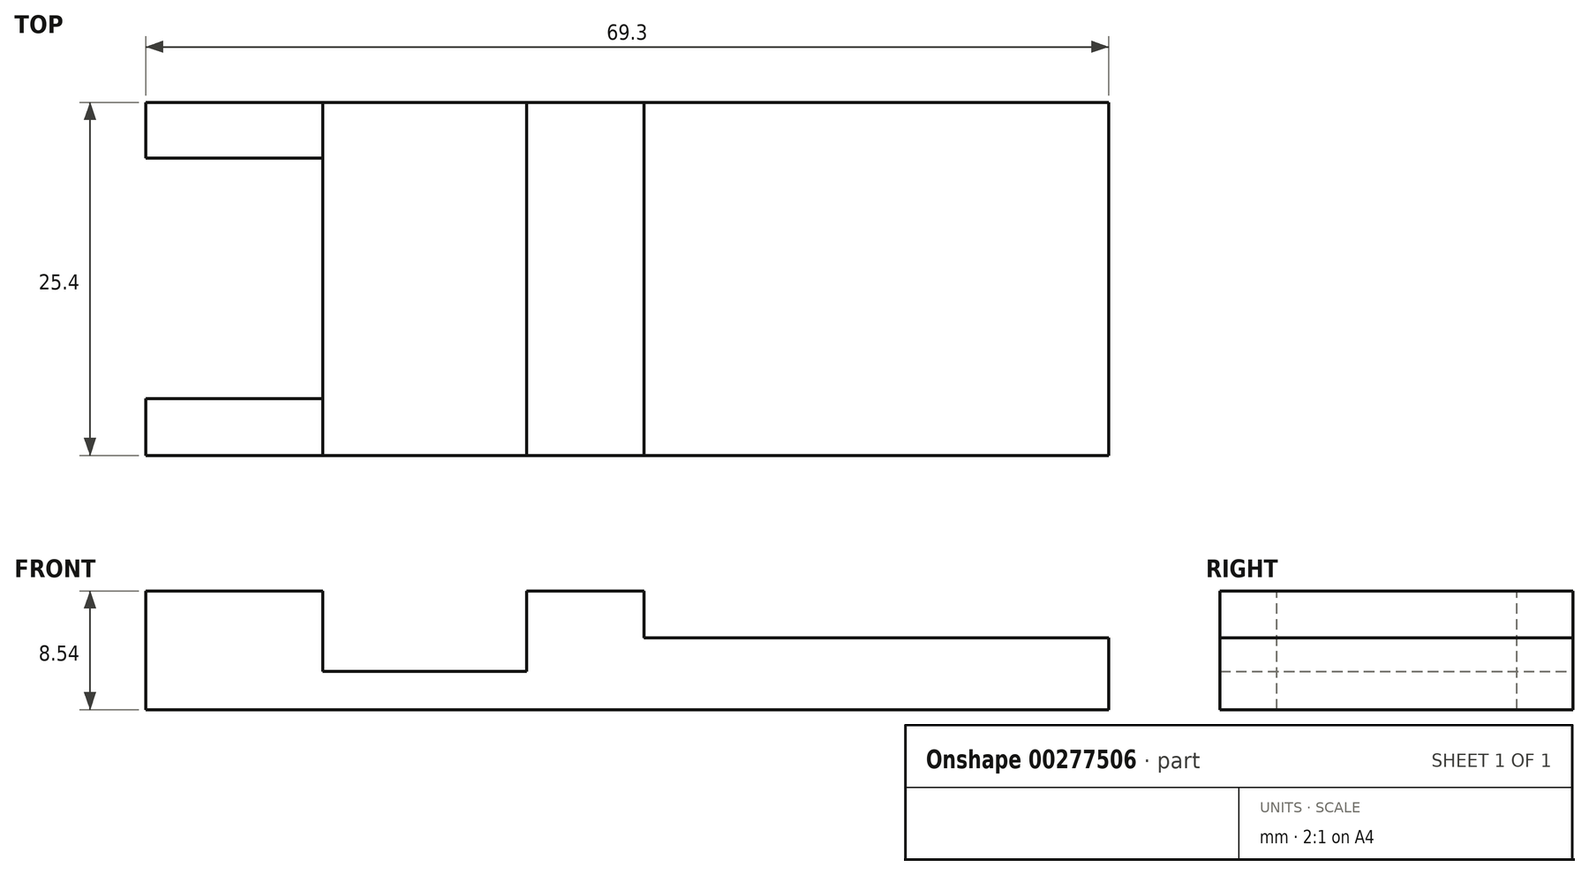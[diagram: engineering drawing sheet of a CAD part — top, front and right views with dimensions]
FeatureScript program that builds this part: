
annotation { "Feature Type Name" : "Feature", "Feature Type Description" : "" }
export const myFeature = defineFeature(function(context is Context, id is Id, definition is map)
    precondition{}
    {
        {
            var Q0;
            Q0=qCreatedBy(makeId("Front.planeOp"),FACE);
            var sketch = newSketch(context, id + "F0", { "sketchPlane" : qUnion([Q0])});
            skLineSegment(sketch, "E0", {"start": v(-49.57, 8.54) * mm, "end": v(-49.57, 0) * mm});
            skLineSegment(sketch, "E1", {"start": v(19.73, 0) * mm, "end": v(19.73, 5.17) * mm});
            skLineSegment(sketch, "E2", {"start": v(19.73, 5.17) * mm, "end": v(-13.72, 5.17) * mm});
            skLineSegment(sketch, "E3", {"start": v(-13.72, 5.17) * mm, "end": v(-13.72, 8.54) * mm});
            skLineSegment(sketch, "E4", {"start": v(-13.72, 8.54) * mm, "end": v(-22.15, 8.54) * mm});
            skLineSegment(sketch, "E5", {"start": v(-22.15, 8.54) * mm, "end": v(-22.15, 2.74) * mm});
            skLineSegment(sketch, "E6", {"start": v(-22.15, 2.74) * mm, "end": v(-36.82, 2.74) * mm});
            skLineSegment(sketch, "E7", {"start": v(-36.82, 2.74) * mm, "end": v(-36.82, 8.54) * mm});
            skLineSegment(sketch, "E8", {"start": v(-36.82, 8.54) * mm, "end": v(-49.57, 8.54) * mm});
            skLineSegment(sketch, "E9", {"start": v(-49.57, 0) * mm, "end": v(19.73, 0) * mm});
            skSolve(sketch);
        }
        {
            var Q0;
            Q0 = qSketchRegion(id + "F0", true);
            extrude(context, id + "F1", {"entities" : qUnion([Q0]), "depth" : 25.4 * mm});
        }
        {
            var Q0;
            Q0=qCreatedBy(makeId("Top.planeOp"),FACE);
            var sketch = newSketch(context, id + "F2", { "sketchPlane" : qUnion([Q0])});
            skLineSegment(sketch, "E10.bottom", {"start": v(-52.98, -4.03) * mm, "end": v(-36.84, -4.03) * mm});
            skLineSegment(sketch, "E10.top", {"start": v(-52.98, -21.32) * mm, "end": v(-36.84, -21.32) * mm});
            skLineSegment(sketch, "E10.left", {"start": v(-52.98, -4.03) * mm, "end": v(-52.98, -21.32) * mm});
            skLineSegment(sketch, "E10.right", {"start": v(-36.84, -4.03) * mm, "end": v(-36.84, -21.32) * mm});
            skSolve(sketch);
        }
        {
            var Q0;
            Q0=makeQuery(id+"F2.imprint","IMPRINT",FACE,{"disambiguationData":[TD([[makeQuery(id+"F2.imprint","IMPRINT",EDGE,{"derivedFrom":sQuery(id+"F2.wireOp",EDGE,"E10.bottom")}),-1.0]])]});
            extrude(context, id + "F3", {"entities" : qUnion([Q0]), "operationType" : NewBodyOperationType.REMOVE, "endBound" : BoundingType.THROUGH_ALL, "depth" : 25.4 * mm});
        }
    });
